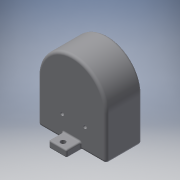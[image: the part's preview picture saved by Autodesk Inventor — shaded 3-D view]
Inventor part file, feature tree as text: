
AUTODESK INVENTOR PART (.ipt)
format: ipt  version: 2018 (Build 220112000, 112)  size: 259,072 bytes
history: native  units: in
note: dims shown in document units (in); Inventor stores cm internally (conversion verified against a paired STEP export)
features: extrude x6, fillet x5, sketch x5, reference x5, plane x1
ambient origin geometry x8: Origin, YZ Plane, XZ Plane, XY Plane, X Axis, Y Axis, Z Axis, Center Point
bodies: Solid1 (feature_tree)
feature tree (22):
  extrude  "Extrusion1"  Depth=0.197in
  extrude  "Extrusion2"  Depth=0.15in
  extrude  "Extrusion3"  Depth=0.4in TaperAngle=0.0deg
  extrude  "Extrusion4"  Depth=0.5in
  extrude  "Extrusion5"  Depth=0.4in TaperAngle=0.0deg
  plane  "Work Plane1"
  extrude  "Extrusion7"  Depth=0.15in
  fillet  "Fillet1"  Radius=0.1378in
  fillet  "Fillet2"  Radius=0.4in
  fillet  "Fillet3"  Radius=0.5in
  fillet  "Fillet4"  Radius=1.9in
  fillet  "Fillet7"  [1 undecoded]
  sketch  "Sketch1"  dims[d1=1.0in d2=0.0in d3=0.197in]
  reference  "Reference1"
  reference  "Reference2"
  sketch  "Sketch2"  dims[d4=0.4in d5=0.0in d6=0.15in]
  reference  "Reference3"
  sketch  "Sketch3"  dims[d7=0.1772in d8=0.4in d9=0.0in]
  sketch  "Sketch5"  dims[d10=0.25in d11=0.5in]
  sketch  "Sketch7"  dims[d12=0.197in d13=0.4in d14=0.0in d15=0.15in d16=0.1378in d17=0.4in d18=0.0in d19=0.5in d20=1.9in d21=-0.95in d28=0.0394in d29=0.098in d30=0.0394in d31=0.098in d32=1.0in d33=0.0in d34=0.0394in d35=0.0394in d36=0.1575in d37=0.1575in d40=0.0394in]
  reference  "Reference4"
  reference  "Reference5"
note: 1 required parameter value undecoded (feature->parameter linkage not recoverable at this tier; creation-order binding heuristic only, values carry confidence <= 0.55)
